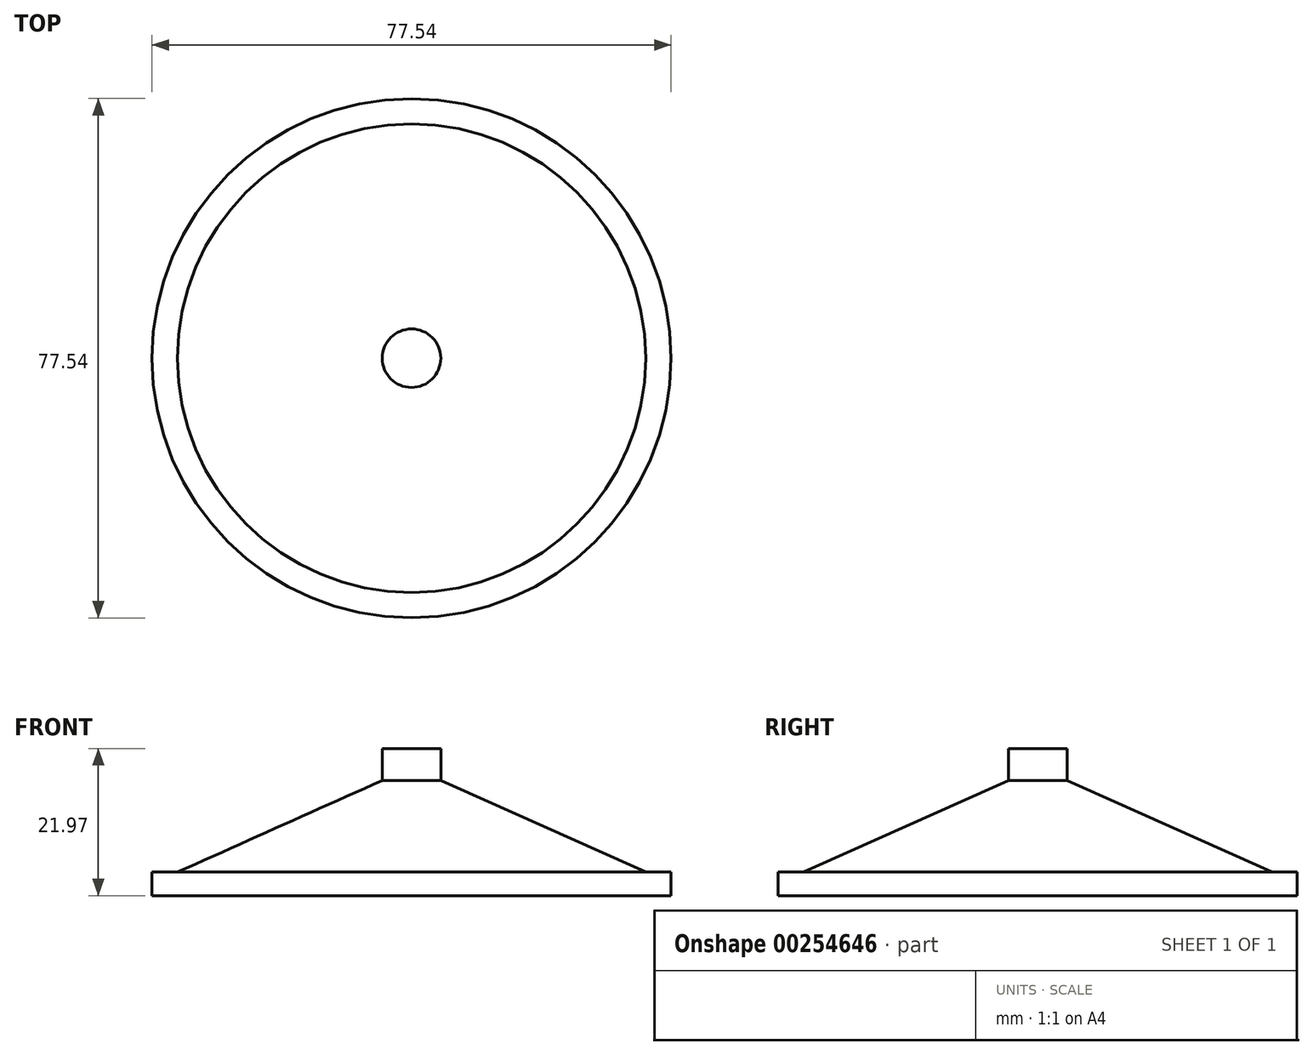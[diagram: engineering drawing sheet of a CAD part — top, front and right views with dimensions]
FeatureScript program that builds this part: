
annotation { "Feature Type Name" : "Feature", "Feature Type Description" : "" }
export const myFeature = defineFeature(function(context is Context, id is Id, definition is map)
    precondition{}
    {
        {
            var Q0;
            Q0=qCreatedBy(makeId("Front.planeOp"),FACE);
            var sketch = newSketch(context, id + "F0", { "sketchPlane" : qUnion([Q0])});
            skLineSegment(sketch, "E0", {"start": v(-4.37, -19.67) * mm, "end": v(-4.37, -22.88) * mm});
            skLineSegment(sketch, "E1", {"start": v(-4.37, -22.88) * mm, "end": v(-34.98, -36.58) * mm});
            skLineSegment(sketch, "E2", {"start": v(-34.98, -36.58) * mm, "end": v(-38.77, -36.58) * mm});
            skLineSegment(sketch, "E3", {"start": v(-38.77, -36.58) * mm, "end": v(-38.77, -40.08) * mm});
            skLineSegment(sketch, "E4", {"start": v(-38.77, -40.08) * mm, "end": v(0, -40.08) * mm});
            skLineSegment(sketch, "E5", {"start": v(0, -40.08) * mm, "end": v(0, -19.67) * mm});
            skLineSegment(sketch, "E6", {"start": v(-4.37, -19.67) * mm, "end": v(-4.37, -18.1) * mm});
            skLineSegment(sketch, "E7", {"start": v(-4.37, -18.1) * mm, "end": v(0, -18.1) * mm});
            skLineSegment(sketch, "E8", {"start": v(0, -18.1) * mm, "end": v(0, -19.67) * mm});
            skSolve(sketch);
        }
        {
            var Q0;
            Q0 = qSketchRegion(id + "F0", true);
            var Q1;
            Q1=sQuery(id+"F0.wireOp",EDGE,"E5");
            revolve(context, id + "F1", {"entities" : qUnion([Q0]), "axis" : qUnion([Q1]), "revolveType" : RevolveType.FULL});
        }
    });
